# Revit family: RN 15087 Systemtrenner BA
name_source: partatom
category: Rohrzubehör
units: mm (PartAtom-declared; Revit-internal decimal feet)

## family parameters
Arbeitsebenenbasiert = Nein
Beim Laden mit Abzugskörper schneiden = Nein
Bemaßung runder Anschluss = Durchmesser verwenden
Gemeinsam genutzt = Nein
Immer vertikal = Ja
Teiletyp = Ventil - Zerlegung in

## types (3) — shared parameters
1.010.00.2 Blattnummer der Richtlinie = 17
1.010.00.3 Ausgabedatum (Monat) der Richtlinie = 201601
1.010.00.4 Herstellername = R. Nussbaum AG
1.010.00.5 Revisionsdatum der Datei = 20190528
1.010.00.6 Webadresse des Herstellers = http://www.nussbaum.ch
1.100.00.3 Sortiernummer für Anzeigereihenfolge = 4
1.100.00.4 Produktbezeichnung = Sicherungs- und Ringleitungsarmaturen
1.960/3L.00.8 Link (URL) = https://www.nussbaum.ch
17.700.00.4 Armaturentyp = 7
17.700.00.7 Maximale Betriebstemperatur TB [°C] = 65
17.700.00.8 Maximaler Betriebsdruck (Arbeitsdruck) ps [1.0 · 105 Pa] = 10
CONNECTOR2_DIAMETER_dZ_0r = 20 mm
CONNECTOR3_DIAMETER_dZ_0r = 20 mm
CONNECTOR4_DIAMETER_dZ_0r = 20 mm
Connector Visibility = Nein
EnclosingSpace Visibility = Nein
Hersteller = R. Nussbauzm AG
URL = https://www.nussbaum.ch

## per-type parameters (varying)
- DN 65: 1.800.00.3 TGA-Nummer=00402900000000000000000000000200700000000000000001???00000; 1.810.00.3 Hersteller-Bestellnummer=15087.23; 1.810.00.4 DATANORM-Nummer=15087.23; 1.810.00.6 GTIN-Nummer=7612945748553; 17.700.00.30 Produktbeschreibung=15087.23, Systemtrenner BA, mit Flanschen, DN=65; 17.700.00.5 Nennweite DN=65; 17.700.00.6 kvs-Wert [m3/h]=36; CONNECTOR0_DIAMETER_dX_0r=65 mm; CONNECTOR0_dX_00=145 mm; CONNECTOR0_dX_01=144 mm; CONNECTOR0_ref_dX=145 mm; CONNECTOR1_DIAMETER_dX_0r=65 mm; CONNECTOR1_dX_00=186 mm; CONNECTOR1_dX_01=187 mm; CONNECTOR1_ref_dX=187 mm; CONNECTOR2_dZ_00=122 mm; CONNECTOR2_dZ_01=147 mm; CONNECTOR2_ref_dX=104 mm; CONNECTOR2_ref_dZ=122 mm; CONNECTOR3_dZ_00=122 mm; CONNECTOR3_dZ_01=147 mm; CONNECTOR3_ref_dX=99 mm; CONNECTOR3_ref_dZ=122 mm; CONNECTOR4_dZ_00=122 mm; CONNECTOR4_dZ_01=147 mm; CONNECTOR4_ref_dX=6 mm  [stored 0.019685 ft]; CONNECTOR4_ref_dZ=122 mm; Modell=15087.23; R. Nussbaum AG 15087.23 de Visibility=Ja; R. Nussbaum AG 15087.24 de Visibility=Nein; R. Nussbaum AG 15087.25 de Visibility=Nein; Typenkommentare=Systemtrenner BADN 65
- DN 80: 1.800.00.3 TGA-Nummer=00402900000000000000000000000200700000000000000002???00000; 1.810.00.3 Hersteller-Bestellnummer=15087.24; 1.810.00.4 DATANORM-Nummer=15087.24; 1.810.00.6 GTIN-Nummer=7612945748720; 17.700.00.30 Produktbeschreibung=15087.24, Systemtrenner BA, mit Flanschen, DN=80; 17.700.00.5 Nennweite DN=80; 17.700.00.6 kvs-Wert [m3/h]=55; CONNECTOR0_DIAMETER_dX_0r=80 mm; CONNECTOR0_dX_00=146 mm; CONNECTOR0_dX_01=145 mm; CONNECTOR0_ref_dX=146 mm; CONNECTOR1_DIAMETER_dX_0r=80 mm; CONNECTOR1_dX_00=205 mm; CONNECTOR1_dX_01=206 mm; CONNECTOR1_ref_dX=206 mm; CONNECTOR2_dZ_00=119 mm; CONNECTOR2_dZ_01=144 mm; CONNECTOR2_ref_dX=105 mm; CONNECTOR2_ref_dZ=119 mm; CONNECTOR3_dZ_00=119 mm; CONNECTOR3_dZ_01=144 mm; CONNECTOR3_ref_dX=98 mm; CONNECTOR3_ref_dZ=119 mm; CONNECTOR4_dZ_00=119 mm; CONNECTOR4_dZ_01=144 mm; CONNECTOR4_ref_dX=7 mm  [stored 0.0229659 ft]; CONNECTOR4_ref_dZ=119 mm; Modell=15087.24; R. Nussbaum AG 15087.23 de Visibility=Nein; R. Nussbaum AG 15087.24 de Visibility=Ja; R. Nussbaum AG 15087.25 de Visibility=Nein; Typenkommentare=Systemtrenner BADN 80
- DN 100: 1.800.00.3 TGA-Nummer=00402900000000000000000000000200700000000000000003???00000; 1.810.00.3 Hersteller-Bestellnummer=15087.25; 1.810.00.4 DATANORM-Nummer=15087.25; 1.810.00.6 GTIN-Nummer=7612945748737; 17.700.00.30 Produktbeschreibung=15087.25, Systemtrenner BA, mit Flanschen, DN=100; 17.700.00.5 Nennweite DN=100; 17.700.00.6 kvs-Wert [m3/h]=85; CONNECTOR0_DIAMETER_dX_0r=100 mm  [stored 0.328084 ft]; CONNECTOR0_dX_00=146 mm; CONNECTOR0_dX_01=145 mm; CONNECTOR0_ref_dX=146 mm; CONNECTOR1_DIAMETER_dX_0r=100 mm  [stored 0.328084 ft]; CONNECTOR1_dX_00=205 mm; CONNECTOR1_dX_01=206 mm; CONNECTOR1_ref_dX=206 mm; CONNECTOR2_dZ_00=130 mm; CONNECTOR2_dZ_01=155 mm; CONNECTOR2_ref_dX=105 mm; CONNECTOR2_ref_dZ=130 mm; CONNECTOR3_dZ_00=130 mm; CONNECTOR3_dZ_01=155 mm; CONNECTOR3_ref_dX=98 mm; CONNECTOR3_ref_dZ=130 mm; CONNECTOR4_dZ_00=130 mm; CONNECTOR4_dZ_01=155 mm; CONNECTOR4_ref_dX=7 mm  [stored 0.0229659 ft]; CONNECTOR4_ref_dZ=130 mm; Modell=15087.25; R. Nussbaum AG 15087.23 de Visibility=Nein; R. Nussbaum AG 15087.24 de Visibility=Nein; R. Nussbaum AG 15087.25 de Visibility=Ja; Typenkommentare=Systemtrenner BADN 100

note: [stored X ft] marks values corroborated as IEEE doubles in the binary element streams (Revit-internal decimal feet)

## geometry (parser evidence)
native form markers: Sweep x1
no freeform markers — native parametric forms only
